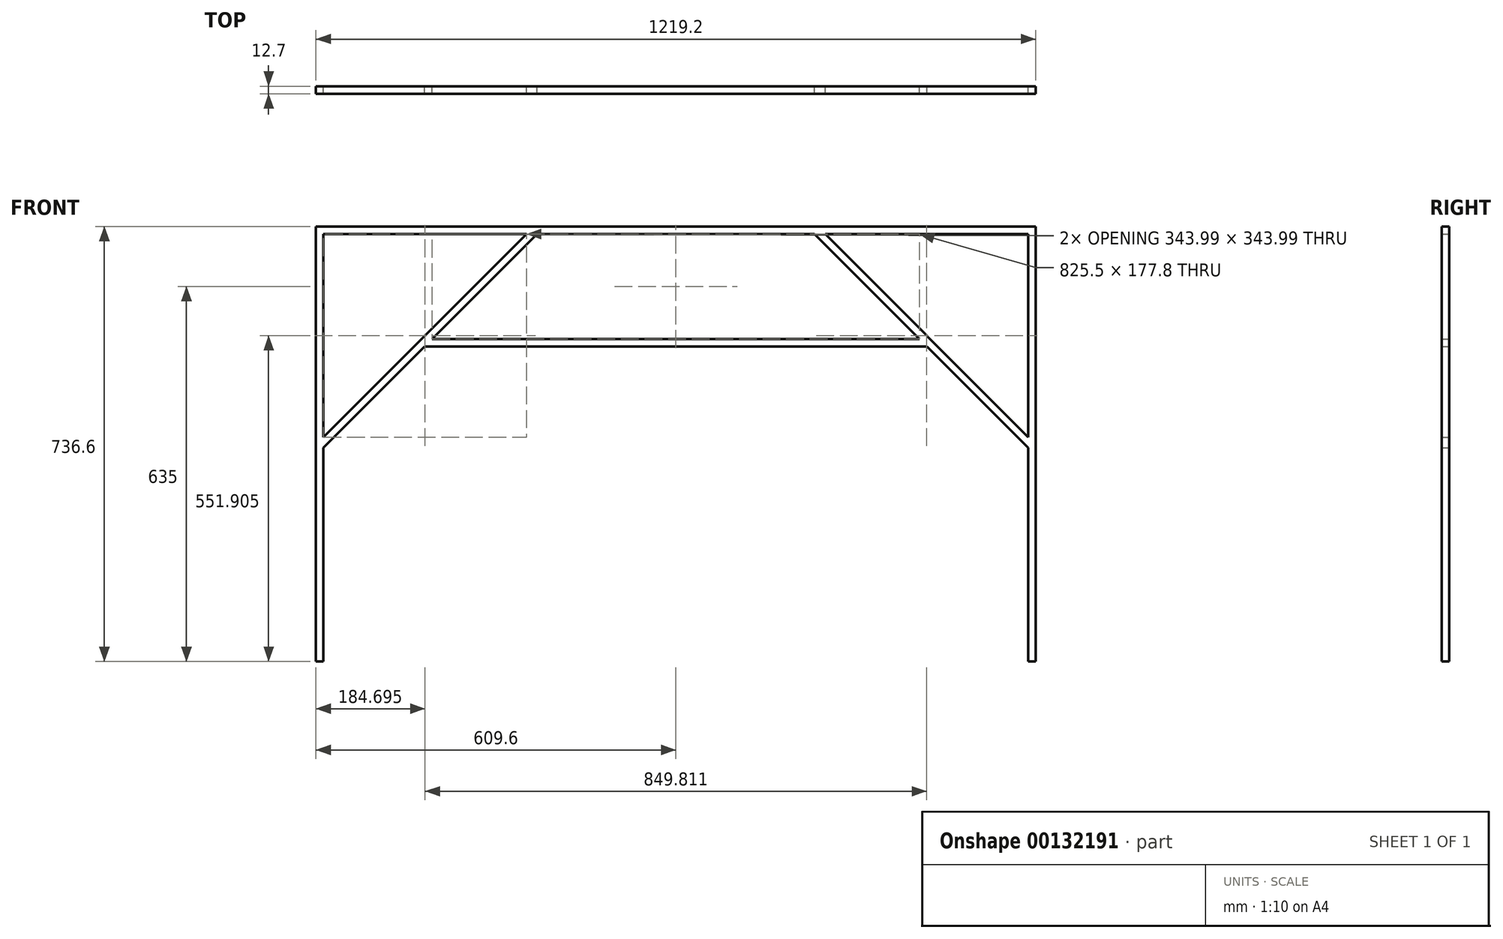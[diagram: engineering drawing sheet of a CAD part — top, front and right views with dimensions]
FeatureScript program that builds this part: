
annotation { "Feature Type Name" : "Feature", "Feature Type Description" : "" }
export const myFeature = defineFeature(function(context is Context, id is Id, definition is map)
    precondition{}
    {
        {
            var Q0;
            Q0=qCreatedBy(makeId("Front.planeOp"),FACE);
            var sketch = newSketch(context, id + "F0", { "sketchPlane" : qUnion([Q0])});
            skLineSegment(sketch, "E0", {"start": v(0, 0) * mm, "end": v(0, 736.6) * mm});
            skLineSegment(sketch, "E1", {"start": v(0, 736.6) * mm, "end": v(1219.2, 736.6) * mm});
            skLineSegment(sketch, "E2", {"start": v(1219.2, 736.6) * mm, "end": v(1219.2, 0) * mm});
            skLineSegment(sketch, "E3.0", {"start": v(1206.5, 723.9) * mm, "end": v(1206.5, 0) * mm});
            skLineSegment(sketch, "E3.1", {"start": v(12.7, 723.9) * mm, "end": v(1206.5, 723.9) * mm});
            skLineSegment(sketch, "E3.2", {"start": v(12.7, 0) * mm, "end": v(12.7, 723.9) * mm});
            skLineSegment(sketch, "E4", {"start": v(0, 0) * mm, "end": v(12.7, 0) * mm});
            skLineSegment(sketch, "E5", {"start": v(1206.5, 0) * mm, "end": v(1219.2, 0) * mm});
            skLineSegment(sketch, "E6", {"start": v(12.7, 361.95) * mm, "end": v(374.65, 723.9) * mm});
            skLineSegment(sketch, "E7", {"start": v(1206.5, 361.95) * mm, "end": v(844.55, 723.9) * mm});
            skLineSegment(sketch, "E8", {"start": v(184.15, 533.4) * mm, "end": v(1035.05, 533.4) * mm});
            skLineSegment(sketch, "E9.0", {"start": v(12.7, 379.91) * mm, "end": v(356.69, 723.9) * mm});
            skLineSegment(sketch, "E10.0", {"start": v(1206.5, 379.91) * mm, "end": v(862.51, 723.9) * mm});
            skLineSegment(sketch, "E11.0", {"start": v(501.67, 546.1) * mm, "end": v(1022.35, 546.1) * mm});
            skLineSegment(sketch, "E12", {"start": v(501.67, 546.1) * mm, "end": v(196.85, 546.1) * mm});
            skSolve(sketch);
        }
        {
            var Q0;
            Q0=makeQuery(id+"F0.imprint","IMPRINT",FACE,{"disambiguationData":[TD([[makeQuery(id+"F0.imprint","IMPRINT",EDGE,{"derivedFrom":sQuery(id+"F0.wireOp",EDGE,"E0")}),-1.0]])]});
            var Q1;
            {var subQ5=sQuery(id+"F0.wireOp",EDGE,"E9.0");Q1=makeQuery(id+"F0.imprint","IMPRINT",FACE,{"disambiguationData":[TD([[makeQuery(id+"F0.imprint","IMPRINT",EDGE,{"derivedFrom":subQ5}),-1.0]])]});}
            var Q2;
            {var subQ3=sQuery(id+"F0.wireOp",EDGE,"E10.0");Q2=makeQuery(id+"F0.imprint","IMPRINT",FACE,{"disambiguationData":[TD([[makeQuery(id+"F0.imprint","IMPRINT",EDGE,{"derivedFrom":subQ3}),1.0]])]});}
            var Q3;
            {var subQ1=sQuery(id+"F0.wireOp",EDGE,"E8");Q3=makeQuery(id+"F0.imprint","IMPRINT",FACE,{"disambiguationData":[TD([[makeQuery(id+"F0.imprint","IMPRINT",EDGE,{"derivedFrom":subQ1}),1.0]])]});}
            extrude(context, id + "F1", {"entities" : qUnion([Q0, Q1, Q2, Q3]), "depth" : 12.7 * mm});
        }
    });
